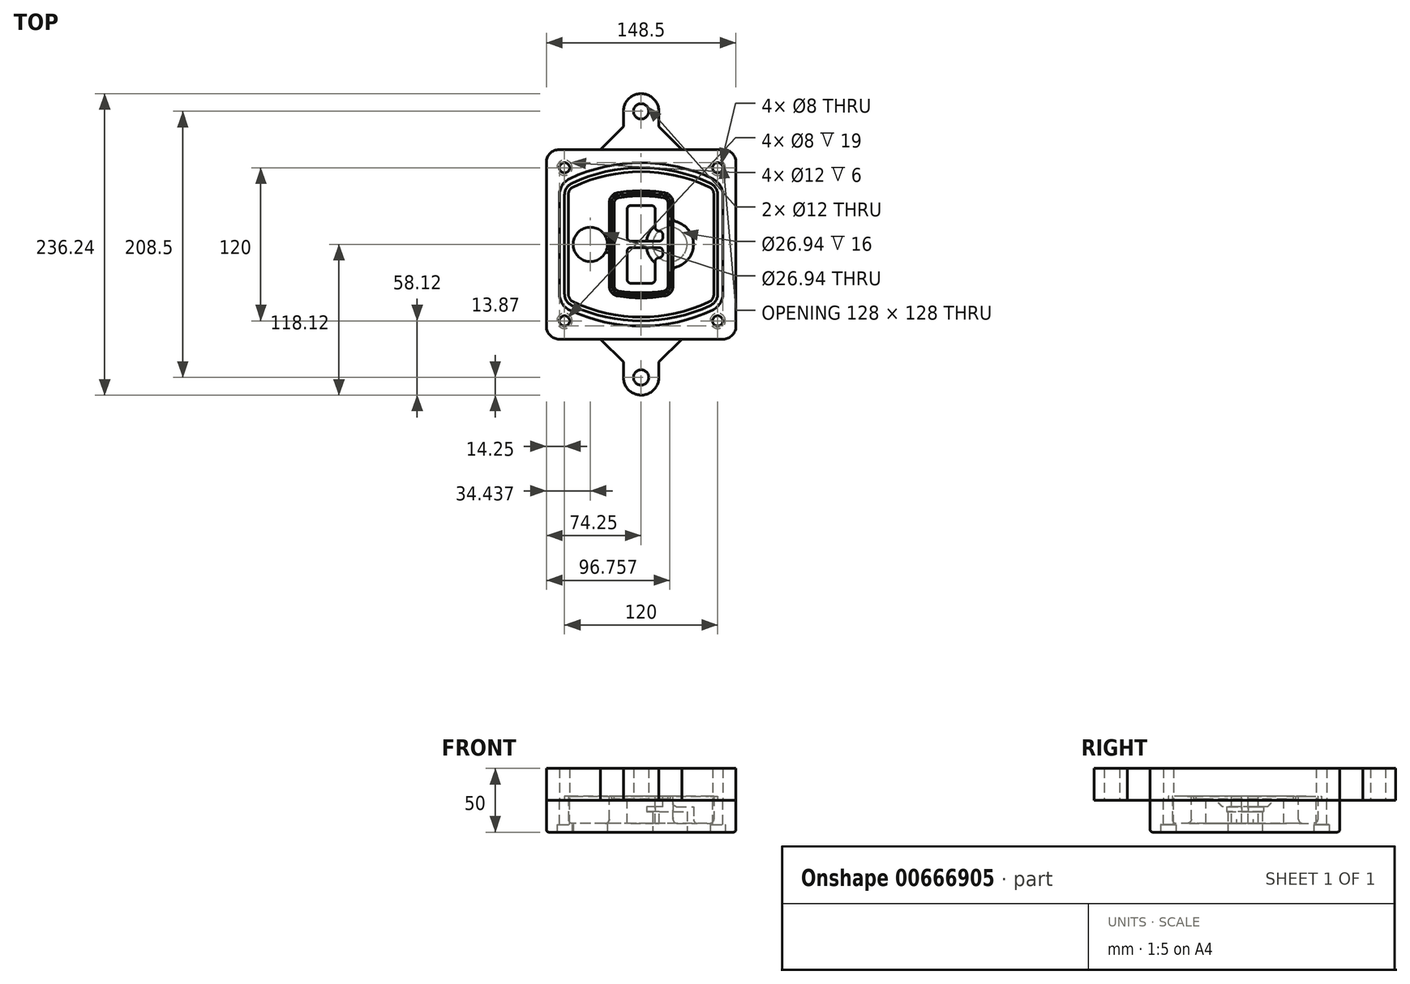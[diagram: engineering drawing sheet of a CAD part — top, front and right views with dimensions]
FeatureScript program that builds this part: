
annotation { "Feature Type Name" : "Feature", "Feature Type Description" : "" }
export const myFeature = defineFeature(function(context is Context, id is Id, definition is map)
    precondition{}
    {
        {
            var Q0;
            Q0=qCreatedBy(makeId("Top.planeOp"),FACE);
            var sketch = newSketch(context, id + "F0", { "sketchPlane" : qUnion([Q0])});
            skPoint(sketch, "E0.rect.middle", {"position": v(0, 0) * mm});
            skLineSegment(sketch, "E1.bottom", {"start": v(-64.25, -74.25) * mm, "end": v(64.25, -74.25) * mm});
            skLineSegment(sketch, "E1.top", {"start": v(-64.25, 74.25) * mm, "end": v(64.25, 74.25) * mm});
            skLineSegment(sketch, "E1.left", {"start": v(-74.25, -64.25) * mm, "end": v(-74.25, 64.25) * mm});
            skLineSegment(sketch, "E1.right", {"start": v(74.25, -64.25) * mm, "end": v(74.25, 64.25) * mm});
            skLineSegment(sketch, "E2", {"start": v(-74.25, 74.25) * mm, "end": v(74.25, -74.25) * mm, "construction": true});
            skLineSegment(sketch, "E3", {"start": v(74.25, 74.25) * mm, "end": v(-74.25, -74.25) * mm, "construction": true});
            skCircle(sketch, "E4", {"center": v(-60, 60) * mm, "radius": 4 * mm});
            skCircle(sketch, "E5", {"center": v(60, 60) * mm, "radius": 4 * mm});
            skCircle(sketch, "E6", {"center": v(60, -60) * mm, "radius": 4 * mm});
            skCircle(sketch, "E7", {"center": v(-60, -60) * mm, "radius": 4 * mm});
            skLineSegment(sketch, "E8", {"start": v(-60, 60) * mm, "end": v(60, 60) * mm, "construction": true});
            skLineSegment(sketch, "E9", {"start": v(60, 60) * mm, "end": v(60, -60) * mm, "construction": true});
            skLineSegment(sketch, "E10", {"start": v(60, -60) * mm, "end": v(-60, -60) * mm, "construction": true});
            skLineSegment(sketch, "E11", {"start": v(-60, -60) * mm, "end": v(-60, 60) * mm, "construction": true});
            skLineSegment(sketch, "E12", {"start": v(-60, 38.83) * mm, "end": v(-60, -38.83) * mm});
            skLineSegment(sketch, "E13", {"start": v(60, 38.83) * mm, "end": v(60, -38.83) * mm});
            skArc(sketch, "E14", {"start": v(54.26, 47.88) * mm, "mid": v(0, 60) * mm, "end": v(-54.26, 47.88) * mm});
            skArc(sketch, "E15", {"start": v(-54.26, -47.88) * mm, "mid": v(0, -60) * mm, "end": v(54.26, -47.88) * mm});
            skLineSegment(sketch, "E16", {"start": v(-60, 0) * mm, "end": v(60, 0) * mm, "construction": true});
            skPoint(sketch, "E17.visualSharp", {"position": v(-60, -45) * mm});
            skArc(sketch, "E17.filletArc", {"start": v(-60, -38.83) * mm, "mid": v(-58.44, -44.2) * mm, "end": v(-54.26, -47.88) * mm});
            skPoint(sketch, "E18.visualSharp", {"position": v(-60, 45) * mm});
            skArc(sketch, "E18.filletArc", {"start": v(-54.26, 47.88) * mm, "mid": v(-58.44, 44.2) * mm, "end": v(-60, 38.83) * mm});
            skPoint(sketch, "E19.visualSharp", {"position": v(60, 45) * mm});
            skArc(sketch, "E19.filletArc", {"start": v(60, 38.83) * mm, "mid": v(58.44, 44.2) * mm, "end": v(54.26, 47.88) * mm});
            skPoint(sketch, "E20.visualSharp", {"position": v(60, -45) * mm});
            skArc(sketch, "E20.filletArc", {"start": v(54.26, -47.88) * mm, "mid": v(58.44, -44.2) * mm, "end": v(60, -38.83) * mm});
            skPoint(sketch, "E21.visualSharp", {"position": v(-74.25, 74.25) * mm});
            skArc(sketch, "E21.filletArc", {"start": v(-64.25, 74.25) * mm, "mid": v(-71.32, 71.32) * mm, "end": v(-74.25, 64.25) * mm});
            skPoint(sketch, "E22.visualSharp", {"position": v(74.25, 74.25) * mm});
            skArc(sketch, "E22.filletArc", {"start": v(74.25, 64.25) * mm, "mid": v(71.32, 71.32) * mm, "end": v(64.25, 74.25) * mm});
            skPoint(sketch, "E23.visualSharp", {"position": v(74.25, -74.25) * mm});
            skArc(sketch, "E23.filletArc", {"start": v(64.25, -74.25) * mm, "mid": v(71.32, -71.32) * mm, "end": v(74.25, -64.25) * mm});
            skPoint(sketch, "E24.visualSharp", {"position": v(-74.25, -74.25) * mm});
            skArc(sketch, "E24.filletArc", {"start": v(-74.25, -64.25) * mm, "mid": v(-71.32, -71.32) * mm, "end": v(-64.25, -74.25) * mm});
            skArc(sketch, "E25.0", {"start": v(57, 38.83) * mm, "mid": v(55.9, 42.58) * mm, "end": v(52.98, 45.17) * mm});
            skLineSegment(sketch, "E25.1", {"start": v(57, 38.83) * mm, "end": v(57, -38.83) * mm});
            skArc(sketch, "E25.2", {"start": v(52.98, -45.17) * mm, "mid": v(55.9, -42.58) * mm, "end": v(57, -38.83) * mm});
            skArc(sketch, "E25.3", {"start": v(-52.98, -45.17) * mm, "mid": v(0, -57) * mm, "end": v(52.98, -45.17) * mm});
            skArc(sketch, "E25.4", {"start": v(-57, -38.83) * mm, "mid": v(-55.9, -42.58) * mm, "end": v(-52.98, -45.17) * mm});
            skArc(sketch, "E25.5", {"start": v(52.98, 45.17) * mm, "mid": v(0, 57) * mm, "end": v(-52.98, 45.17) * mm});
            skLineSegment(sketch, "E25.6", {"start": v(-57, 38.83) * mm, "end": v(-57, -38.83) * mm});
            skArc(sketch, "E25.7", {"start": v(-52.98, 45.17) * mm, "mid": v(-55.9, 42.58) * mm, "end": v(-57, 38.83) * mm});
            skArc(sketch, "E26.0", {"start": v(-55.96, 51.5) * mm, "mid": v(-61.82, 46.33) * mm, "end": v(-64, 38.83) * mm});
            skArc(sketch, "E26.1", {"start": v(55.96, 51.5) * mm, "mid": v(0, 64) * mm, "end": v(-55.96, 51.5) * mm});
            skArc(sketch, "E26.2", {"start": v(64, 38.83) * mm, "mid": v(61.82, 46.33) * mm, "end": v(55.96, 51.5) * mm});
            skLineSegment(sketch, "E26.3", {"start": v(64, 38.83) * mm, "end": v(64, -38.83) * mm});
            skArc(sketch, "E26.4", {"start": v(55.96, -51.5) * mm, "mid": v(61.82, -46.33) * mm, "end": v(64, -38.83) * mm});
            skLineSegment(sketch, "E26.5", {"start": v(-64, 38.83) * mm, "end": v(-64, -38.83) * mm});
            skArc(sketch, "E26.6", {"start": v(-55.96, -51.5) * mm, "mid": v(0, -64) * mm, "end": v(55.96, -51.5) * mm});
            skArc(sketch, "E26.7", {"start": v(-64, -38.83) * mm, "mid": v(-61.82, -46.33) * mm, "end": v(-55.96, -51.5) * mm});
            skSolve(sketch);
        }
        {
            var Q0;
            Q0=makeQuery(id+"F0.imprint","IMPRINT",FACE,{"disambiguationData":[TD([[makeQuery(id+"F0.imprint","IMPRINT",EDGE,{"derivedFrom":sQuery(id+"F0.wireOp",EDGE,"E1.bottom")}),1.0]])]});
            var Q1;
            Q1=makeQuery(id+"F0.imprint","IMPRINT",FACE,{"disambiguationData":[TD([[makeQuery(id+"F0.imprint","IMPRINT",EDGE,{"derivedFrom":sQuery(id+"F0.wireOp",EDGE,"E12")}),1.0]])]});
            var Q2;
            Q2=makeQuery(id+"F0.imprint","IMPRINT",FACE,{"disambiguationData":[TD([[makeQuery(id+"F0.imprint","IMPRINT",EDGE,{"derivedFrom":sQuery(id+"F0.wireOp",EDGE,"E25.0")}),1.0]])]});
            var Q3;
            Q3=makeQuery(id+"F0.imprint","IMPRINT",FACE,{"disambiguationData":[TD([[makeQuery(id+"F0.imprint","IMPRINT",EDGE,{"derivedFrom":sQuery(id+"F0.wireOp",EDGE,"E12")}),-1.0]])]});
            extrude(context, id + "F1", {"entities" : qUnion([Q0, Q1, Q2, Q3]), "oppositeDirection" : true, "depth" : 25 * mm});
        }
        {
            var Q0;
            Q0=makeQuery(id+"F0.imprint","IMPRINT",FACE,{"disambiguationData":[TD([[makeQuery(id+"F0.imprint","IMPRINT",EDGE,{"derivedFrom":sQuery(id+"F0.wireOp",EDGE,"E12")}),1.0]])]});
            extrude(context, id + "F2", {"entities" : qUnion([Q0]), "operationType" : NewBodyOperationType.ADD, "depth" : 3 * mm});
        }
        {
            var Q0;
            Q0=makeQuery(id+"F0.imprint","IMPRINT",FACE,{"disambiguationData":[TD([[makeQuery(id+"F0.imprint","IMPRINT",EDGE,{"derivedFrom":sQuery(id+"F0.wireOp",EDGE,"E25.0")}),1.0]])]});
            extrude(context, id + "F3", {"entities" : qUnion([Q0]), "operationType" : NewBodyOperationType.REMOVE, "oppositeDirection" : true, "depth" : 18 * mm});
        }
        {
            var Q0;
            Q0=makeQuery(id+"F2.opExtrude","CAP_FACE",FACE,{"disambiguationData":[OSD([sQuery(id+"F0.wireOp",EDGE,"E12"),sQuery(id+"F0.wireOp",EDGE,"E13"),sQuery(id+"F0.wireOp",EDGE,"E14"),sQuery(id+"F0.wireOp",EDGE,"E15"),sQuery(id+"F0.wireOp",EDGE,"E17.filletArc"),sQuery(id+"F0.wireOp",EDGE,"E18.filletArc"),sQuery(id+"F0.wireOp",EDGE,"E19.filletArc"),sQuery(id+"F0.wireOp",EDGE,"E20.filletArc"),sQuery(id+"F0.wireOp",EDGE,"E25.0"),sQuery(id+"F0.wireOp",EDGE,"E25.1"),sQuery(id+"F0.wireOp",EDGE,"E25.2"),sQuery(id+"F0.wireOp",EDGE,"E25.3"),sQuery(id+"F0.wireOp",EDGE,"E25.4"),sQuery(id+"F0.wireOp",EDGE,"E25.5"),sQuery(id+"F0.wireOp",EDGE,"E25.6"),sQuery(id+"F0.wireOp",EDGE,"E25.7")])],"isStart":false});
            var sketch = newSketch(context, id + "F4", { "sketchPlane" : qUnion([Q0])});
            skArc(sketch, "E27.0", {"start": v(-18.34, -40.45) * mm, "mid": v(0, -42) * mm, "end": v(18.34, -40.45) * mm});
            skArc(sketch, "E28.0", {"start": v(18.34, 40.45) * mm, "mid": v(0, 42) * mm, "end": v(-18.34, 40.45) * mm});
            skLineSegment(sketch, "E29", {"start": v(-25, 32.57) * mm, "end": v(-25, -32.57) * mm});
            skLineSegment(sketch, "E30", {"start": v(25, 32.57) * mm, "end": v(25, -32.57) * mm});
            skLineSegment(sketch, "E31", {"start": v(-25, 39.1) * mm, "end": v(25, 39.1) * mm, "construction": true});
            skLineSegment(sketch, "E32", {"start": v(-25, -39.1) * mm, "end": v(25, -39.1) * mm, "construction": true});
            skPoint(sketch, "E33.visualSharp", {"position": v(-25, 39.1) * mm});
            skArc(sketch, "E33.filletArc", {"start": v(-18.34, 40.45) * mm, "mid": v(-23.11, 37.73) * mm, "end": v(-25, 32.57) * mm});
            skPoint(sketch, "E34.visualSharp", {"position": v(25, 39.1) * mm});
            skArc(sketch, "E34.filletArc", {"start": v(25, 32.57) * mm, "mid": v(23.11, 37.73) * mm, "end": v(18.34, 40.45) * mm});
            skPoint(sketch, "E35.visualSharp", {"position": v(25, -39.1) * mm});
            skArc(sketch, "E35.filletArc", {"start": v(18.34, -40.45) * mm, "mid": v(23.11, -37.73) * mm, "end": v(25, -32.57) * mm});
            skPoint(sketch, "E36.visualSharp", {"position": v(-25, -39.1) * mm});
            skArc(sketch, "E36.filletArc", {"start": v(-25, -32.57) * mm, "mid": v(-23.11, -37.73) * mm, "end": v(-18.34, -40.45) * mm});
            skArc(sketch, "E37.0", {"start": v(52.98, 45.17) * mm, "mid": v(0, 57) * mm, "end": v(-52.98, 45.17) * mm});
            skArc(sketch, "E37.1", {"start": v(-52.98, 45.17) * mm, "mid": v(-55.9, 42.58) * mm, "end": v(-57, 38.83) * mm});
            skLineSegment(sketch, "E37.2", {"start": v(-57, 38.83) * mm, "end": v(-57, -38.83) * mm});
            skArc(sketch, "E37.3", {"start": v(-57, -38.83) * mm, "mid": v(-55.9, -42.58) * mm, "end": v(-52.98, -45.17) * mm});
            skArc(sketch, "E37.4", {"start": v(-52.98, -45.17) * mm, "mid": v(0, -57) * mm, "end": v(52.98, -45.17) * mm});
            skArc(sketch, "E37.5", {"start": v(52.98, -45.17) * mm, "mid": v(55.9, -42.58) * mm, "end": v(57, -38.83) * mm});
            skLineSegment(sketch, "E37.6", {"start": v(57, 38.83) * mm, "end": v(57, -38.83) * mm});
            skArc(sketch, "E37.7", {"start": v(57, 38.83) * mm, "mid": v(55.9, 42.58) * mm, "end": v(52.98, 45.17) * mm});
            skLineSegment(sketch, "E38.0", {"start": v(23, 32.57) * mm, "end": v(23, -32.57) * mm});
            skArc(sketch, "E38.1", {"start": v(18, -38.48) * mm, "mid": v(21.58, -36.44) * mm, "end": v(23, -32.57) * mm});
            skArc(sketch, "E38.2", {"start": v(-18, -38.48) * mm, "mid": v(0, -40) * mm, "end": v(18, -38.48) * mm});
            skArc(sketch, "E38.3", {"start": v(-23, -32.57) * mm, "mid": v(-21.58, -36.44) * mm, "end": v(-18, -38.48) * mm});
            skLineSegment(sketch, "E38.4", {"start": v(-23, 32.57) * mm, "end": v(-23, -32.57) * mm});
            skArc(sketch, "E38.5", {"start": v(23, 32.57) * mm, "mid": v(21.58, 36.44) * mm, "end": v(18, 38.48) * mm});
            skArc(sketch, "E38.6", {"start": v(-18, 38.48) * mm, "mid": v(-21.58, 36.44) * mm, "end": v(-23, 32.57) * mm});
            skArc(sketch, "E38.7", {"start": v(18, 38.48) * mm, "mid": v(0, 40) * mm, "end": v(-18, 38.48) * mm});
            skArc(sketch, "E39.0", {"start": v(21, 32.57) * mm, "mid": v(20.06, 35.15) * mm, "end": v(17.67, 36.5) * mm});
            skLineSegment(sketch, "E39.1", {"start": v(21, 32.57) * mm, "end": v(21, -32.57) * mm});
            skArc(sketch, "E39.2", {"start": v(17.67, -36.5) * mm, "mid": v(20.06, -35.15) * mm, "end": v(21, -32.57) * mm});
            skArc(sketch, "E39.3", {"start": v(-17.67, -36.5) * mm, "mid": v(0, -38) * mm, "end": v(17.67, -36.5) * mm});
            skArc(sketch, "E39.4", {"start": v(-21, -32.57) * mm, "mid": v(-20.06, -35.15) * mm, "end": v(-17.67, -36.5) * mm});
            skArc(sketch, "E39.5", {"start": v(17.67, 36.5) * mm, "mid": v(0, 38) * mm, "end": v(-17.67, 36.5) * mm});
            skLineSegment(sketch, "E39.6", {"start": v(-21, 32.57) * mm, "end": v(-21, -32.57) * mm});
            skArc(sketch, "E39.7", {"start": v(-17.67, 36.5) * mm, "mid": v(-20.06, 35.15) * mm, "end": v(-21, 32.57) * mm});
            skLineSegment(sketch, "E40", {"start": v(-25, 0) * mm, "end": v(25, 0) * mm, "construction": true});
            skLineSegment(sketch, "E41", {"start": v(-11, 5.5) * mm, "end": v(-11, 27.5) * mm});
            skLineSegment(sketch, "E42", {"start": v(-8, 30.5) * mm, "end": v(8, 30.5) * mm});
            skLineSegment(sketch, "E43", {"start": v(11, 27.5) * mm, "end": v(11, 13.5) * mm});
            skLineSegment(sketch, "E44", {"start": v(14, 10.5) * mm, "end": v(14, 10.5) * mm});
            skLineSegment(sketch, "E45", {"start": v(17, 7.5) * mm, "end": v(17, 5.5) * mm});
            skLineSegment(sketch, "E46", {"start": v(14, 2.5) * mm, "end": v(-8, 2.5) * mm});
            skPoint(sketch, "E47.visualSharp", {"position": v(-11, 30.5) * mm});
            skArc(sketch, "E47.filletArc", {"start": v(-8, 30.5) * mm, "mid": v(-10.12, 29.62) * mm, "end": v(-11, 27.5) * mm});
            skPoint(sketch, "E48.visualSharp", {"position": v(11, 30.5) * mm});
            skArc(sketch, "E48.filletArc", {"start": v(11, 27.5) * mm, "mid": v(10.12, 29.62) * mm, "end": v(8, 30.5) * mm});
            skPoint(sketch, "E49.visualSharp", {"position": v(11, 10.5) * mm});
            skArc(sketch, "E49.filletArc", {"start": v(11, 13.5) * mm, "mid": v(11.88, 11.38) * mm, "end": v(14, 10.5) * mm});
            skPoint(sketch, "E50.visualSharp", {"position": v(17, 10.5) * mm});
            skArc(sketch, "E50.filletArc", {"start": v(17, 7.5) * mm, "mid": v(16.12, 9.62) * mm, "end": v(14, 10.5) * mm});
            skPoint(sketch, "E51.visualSharp", {"position": v(17, 2.5) * mm});
            skArc(sketch, "E51.filletArc", {"start": v(14, 2.5) * mm, "mid": v(16.12, 3.38) * mm, "end": v(17, 5.5) * mm});
            skPoint(sketch, "E52.visualSharp", {"position": v(-11, 2.5) * mm});
            skArc(sketch, "E52.filletArc", {"start": v(-11, 5.5) * mm, "mid": v(-10.12, 3.38) * mm, "end": v(-8, 2.5) * mm});
            skLineSegment(sketch, "E53.0.MirrorCS", {"start": v(14, -2.5) * mm, "end": v(-8, -2.5) * mm});
            skArc(sketch, "E54.0.MirrorCS", {"start": v(-11, -5.5) * mm, "mid": v(-10.12, -3.38) * mm, "end": v(-8, -2.5) * mm});
            skLineSegment(sketch, "E55.0.MirrorCS", {"start": v(-11, -5.5) * mm, "end": v(-11, -27.5) * mm});
            skArc(sketch, "E56.0.MirrorCS", {"start": v(-8, -30.5) * mm, "mid": v(-10.12, -29.62) * mm, "end": v(-11, -27.5) * mm});
            skLineSegment(sketch, "E57.0.MirrorCS", {"start": v(-8, -30.5) * mm, "end": v(8, -30.5) * mm});
            skArc(sketch, "E58.0.MirrorCS", {"start": v(11, -27.5) * mm, "mid": v(10.12, -29.62) * mm, "end": v(8, -30.5) * mm});
            skLineSegment(sketch, "E59.0.MirrorCS", {"start": v(11, -27.5) * mm, "end": v(11, -13.5) * mm});
            skArc(sketch, "E60.0.MirrorCS", {"start": v(11, -13.5) * mm, "mid": v(11.88, -11.38) * mm, "end": v(14, -10.5) * mm});
            skArc(sketch, "E61.0.MirrorCS", {"start": v(17, -7.5) * mm, "mid": v(16.12, -9.62) * mm, "end": v(14, -10.5) * mm});
            skLineSegment(sketch, "E62.0.MirrorCS", {"start": v(17, -7.5) * mm, "end": v(17, -5.5) * mm});
            skArc(sketch, "E63.0.MirrorCS", {"start": v(14, -2.5) * mm, "mid": v(16.12, -3.38) * mm, "end": v(17, -5.5) * mm});
            skSolve(sketch);
        }
        {
            var Q0;
            Q0=makeQuery(id+"F4.imprint","IMPRINT",FACE,{"disambiguationData":[TD([[makeQuery(id+"F4.imprint","IMPRINT",EDGE,{"derivedFrom":sQuery(id+"F4.wireOp",EDGE,"E27.0")}),1.0]])]});
            var Q1;
            Q1=makeQuery(id+"F4.imprint","IMPRINT",FACE,{"disambiguationData":[TD([[makeQuery(id+"F4.imprint","IMPRINT",EDGE,{"derivedFrom":sQuery(id+"F4.wireOp",EDGE,"E38.0")}),-1.0]])]});
            var Q2;
            Q2=makeQuery(id+"F4.imprint","IMPRINT",FACE,{"disambiguationData":[TD([[makeQuery(id+"F4.imprint","IMPRINT",EDGE,{"derivedFrom":sQuery(id+"F4.wireOp",EDGE,"E39.0")}),1.0]])]});
            extrude(context, id + "F5", {"entities" : qUnion([Q0, Q1, Q2]), "operationType" : NewBodyOperationType.ADD, "endBound" : BoundingType.UP_TO_NEXT, "oppositeDirection" : true, "depth" : 25 * mm});
        }
        {
            var Q0;
            Q0=makeQuery(id+"F4.imprint","IMPRINT",FACE,{"disambiguationData":[TD([[makeQuery(id+"F4.imprint","IMPRINT",EDGE,{"derivedFrom":sQuery(id+"F4.wireOp",EDGE,"E38.0")}),-1.0]])]});
            extrude(context, id + "F6", {"entities" : qUnion([Q0]), "operationType" : NewBodyOperationType.REMOVE, "oppositeDirection" : true, "depth" : 2 * mm});
        }
        {
            var Q0;
            Q0=makeQuery(id+"F1.opExtrude","CAP_FACE",FACE,{"disambiguationData":[OSD([sQuery(id+"F0.wireOp",EDGE,"E1.bottom"),sQuery(id+"F0.wireOp",EDGE,"E1.top"),sQuery(id+"F0.wireOp",EDGE,"E1.left"),sQuery(id+"F0.wireOp",EDGE,"E1.right"),sQuery(id+"F0.wireOp",EDGE,"E4"),sQuery(id+"F0.wireOp",EDGE,"E5"),sQuery(id+"F0.wireOp",EDGE,"E6"),sQuery(id+"F0.wireOp",EDGE,"E7"),sQuery(id+"F0.wireOp",EDGE,"E21.filletArc"),sQuery(id+"F0.wireOp",EDGE,"E22.filletArc"),sQuery(id+"F0.wireOp",EDGE,"E23.filletArc"),sQuery(id+"F0.wireOp",EDGE,"E24.filletArc")])],"isStart":false});
            var sketch = newSketch(context, id + "F7", { "sketchPlane" : qUnion([Q0])});
            skCircle(sketch, "E64", {"center": v(22.5, 0) * mm, "radius": 13.47 * mm});
            skCircle(sketch, "E65", {"center": v(-39.81, 0) * mm, "radius": 13.47 * mm});
            skLineSegment(sketch, "E66", {"start": v(74.25, 0) * mm, "end": v(-74.25, 0) * mm});
            skCircle(sketch, "E67", {"center": v(22.5, 0) * mm, "radius": 18.47 * mm});
            skCircle(sketch, "E68", {"center": v(60, -60) * mm, "radius": 6 * mm});
            skCircle(sketch, "E69", {"center": v(-60, -60) * mm, "radius": 6 * mm});
            skCircle(sketch, "E70", {"center": v(-60, 60) * mm, "radius": 6 * mm});
            skCircle(sketch, "E71", {"center": v(60, 60) * mm, "radius": 6 * mm});
            skSolve(sketch);
        }
        {
            var Q0;
            {var subQ1=sQuery(id+"F7.wireOp",EDGE,"E66");var subQ4=sQuery(id+"F7.wireOp",EDGE,"E64");var subQ6=makeQuery(id+"F7.imprint","INTERSECT",VERTEX,{"disambiguationData":[OD(0.0)],"derivedFrom":[subQ4,subQ1]});Q0=makeQuery(id+"F7.imprint","IMPRINT",FACE,{"disambiguationData":[TD([[makeQuery(id+"F7.imprint","IMPRINT",EDGE,{"disambiguationData":[TD([[subQ6,-1.0]])],"derivedFrom":subQ4}),-1.0]])]});}
            var Q1;
            {var subQ0=sQuery(id+"F7.wireOp",EDGE,"E66");var subQ1=sQuery(id+"F7.wireOp",EDGE,"E64");var subQ3=makeQuery(id+"F7.imprint","INTERSECT",VERTEX,{"disambiguationData":[OD(0.0)],"derivedFrom":[subQ1,subQ0]});Q1=makeQuery(id+"F7.imprint","IMPRINT",FACE,{"disambiguationData":[TD([[makeQuery(id+"F7.imprint","IMPRINT",EDGE,{"disambiguationData":[TD([[subQ3,-1.0]])],"derivedFrom":subQ1}),1.0]])]});}
            var Q2;
            {var subQ0=sQuery(id+"F7.wireOp",EDGE,"E66");var subQ1=sQuery(id+"F7.wireOp",EDGE,"E64");var subQ3=makeQuery(id+"F7.imprint","INTERSECT",VERTEX,{"disambiguationData":[OD(0.0)],"derivedFrom":[subQ1,subQ0]});Q2=makeQuery(id+"F7.imprint","IMPRINT",FACE,{"disambiguationData":[TD([[makeQuery(id+"F7.imprint","IMPRINT",EDGE,{"disambiguationData":[TD([[subQ3,1.0]])],"derivedFrom":subQ1}),1.0]])]});}
            var Q3;
            {var subQ1=sQuery(id+"F7.wireOp",EDGE,"E66");var subQ4=sQuery(id+"F7.wireOp",EDGE,"E64");var subQ6=makeQuery(id+"F7.imprint","INTERSECT",VERTEX,{"disambiguationData":[OD(0.0)],"derivedFrom":[subQ4,subQ1]});Q3=makeQuery(id+"F7.imprint","IMPRINT",FACE,{"disambiguationData":[TD([[makeQuery(id+"F7.imprint","IMPRINT",EDGE,{"disambiguationData":[TD([[subQ6,1.0]])],"derivedFrom":subQ4}),-1.0]])]});}
            extrude(context, id + "F8", {"entities" : qUnion([Q0, Q1, Q2, Q3]), "operationType" : NewBodyOperationType.ADD, "oppositeDirection" : true, "depth" : 20 * mm});
        }
        {
            var Q0;
            {var subQ0=sQuery(id+"F7.wireOp",EDGE,"E66");var subQ1=sQuery(id+"F7.wireOp",EDGE,"E64");var subQ3=makeQuery(id+"F7.imprint","INTERSECT",VERTEX,{"disambiguationData":[OD(0.0)],"derivedFrom":[subQ1,subQ0]});Q0=makeQuery(id+"F7.imprint","IMPRINT",FACE,{"disambiguationData":[TD([[makeQuery(id+"F7.imprint","IMPRINT",EDGE,{"disambiguationData":[TD([[subQ3,-1.0]])],"derivedFrom":subQ1}),1.0]])]});}
            var Q1;
            {var subQ0=sQuery(id+"F7.wireOp",EDGE,"E66");var subQ1=sQuery(id+"F7.wireOp",EDGE,"E64");var subQ3=makeQuery(id+"F7.imprint","INTERSECT",VERTEX,{"disambiguationData":[OD(0.0)],"derivedFrom":[subQ1,subQ0]});Q1=makeQuery(id+"F7.imprint","IMPRINT",FACE,{"disambiguationData":[TD([[makeQuery(id+"F7.imprint","IMPRINT",EDGE,{"disambiguationData":[TD([[subQ3,1.0]])],"derivedFrom":subQ1}),1.0]])]});}
            extrude(context, id + "F9", {"entities" : qUnion([Q0, Q1]), "operationType" : NewBodyOperationType.REMOVE, "oppositeDirection" : true, "depth" : 16 * mm});
        }
        {
            var Q0;
            {var subQ0=sQuery(id+"F7.wireOp",EDGE,"E66");var subQ1=sQuery(id+"F7.wireOp",EDGE,"E65");var subQ3=makeQuery(id+"F7.imprint","INTERSECT",VERTEX,{"disambiguationData":[OD(0.0)],"derivedFrom":[subQ1,subQ0]});Q0=makeQuery(id+"F7.imprint","IMPRINT",FACE,{"disambiguationData":[TD([[makeQuery(id+"F7.imprint","IMPRINT",EDGE,{"disambiguationData":[TD([[subQ3,-1.0]])],"derivedFrom":subQ1}),1.0]])]});}
            var Q1;
            {var subQ0=sQuery(id+"F7.wireOp",EDGE,"E66");var subQ1=sQuery(id+"F7.wireOp",EDGE,"E65");var subQ3=makeQuery(id+"F7.imprint","INTERSECT",VERTEX,{"disambiguationData":[OD(0.0)],"derivedFrom":[subQ1,subQ0]});Q1=makeQuery(id+"F7.imprint","IMPRINT",FACE,{"disambiguationData":[TD([[makeQuery(id+"F7.imprint","IMPRINT",EDGE,{"disambiguationData":[TD([[subQ3,1.0]])],"derivedFrom":subQ1}),1.0]])]});}
            extrude(context, id + "F10", {"entities" : qUnion([Q0, Q1]), "operationType" : NewBodyOperationType.REMOVE, "oppositeDirection" : true, "depth" : 25 * mm});
        }
        {
            var Q0;
            Q0=makeQuery(id+"F7.imprint","IMPRINT",FACE,{"disambiguationData":[TD([[makeQuery(id+"F7.imprint","IMPRINT",EDGE,{"derivedFrom":sQuery(id+"F7.wireOp",EDGE,"E68")}),1.0]])]});
            var Q1;
            Q1=makeQuery(id+"F7.imprint","IMPRINT",FACE,{"disambiguationData":[TD([[makeQuery(id+"F7.imprint","IMPRINT",EDGE,{"derivedFrom":makeQuery(id+"F1.opExtrude","CAP_EDGE",EDGE,{"disambiguationData":[OSD([sQuery(id+"F0.wireOp",EDGE,"E5")])],"isStart":false})}),-1.0]])]});
            var Q2;
            Q2=makeQuery(id+"F7.imprint","IMPRINT",FACE,{"disambiguationData":[TD([[makeQuery(id+"F7.imprint","IMPRINT",EDGE,{"derivedFrom":sQuery(id+"F7.wireOp",EDGE,"E69")}),1.0]])]});
            var Q3;
            Q3=makeQuery(id+"F7.imprint","IMPRINT",FACE,{"disambiguationData":[TD([[makeQuery(id+"F7.imprint","IMPRINT",EDGE,{"derivedFrom":makeQuery(id+"F1.opExtrude","CAP_EDGE",EDGE,{"disambiguationData":[OSD([sQuery(id+"F0.wireOp",EDGE,"E4")])],"isStart":false})}),-1.0]])]});
            var Q4;
            Q4=makeQuery(id+"F7.imprint","IMPRINT",FACE,{"disambiguationData":[TD([[makeQuery(id+"F7.imprint","IMPRINT",EDGE,{"derivedFrom":sQuery(id+"F7.wireOp",EDGE,"E70")}),1.0]])]});
            var Q5;
            Q5=makeQuery(id+"F7.imprint","IMPRINT",FACE,{"disambiguationData":[TD([[makeQuery(id+"F7.imprint","IMPRINT",EDGE,{"derivedFrom":makeQuery(id+"F1.opExtrude","CAP_EDGE",EDGE,{"disambiguationData":[OSD([sQuery(id+"F0.wireOp",EDGE,"E7")])],"isStart":false})}),-1.0]])]});
            var Q6;
            Q6=makeQuery(id+"F7.imprint","IMPRINT",FACE,{"disambiguationData":[TD([[makeQuery(id+"F7.imprint","IMPRINT",EDGE,{"derivedFrom":sQuery(id+"F7.wireOp",EDGE,"E71")}),1.0]])]});
            var Q7;
            Q7=makeQuery(id+"F7.imprint","IMPRINT",FACE,{"disambiguationData":[TD([[makeQuery(id+"F7.imprint","IMPRINT",EDGE,{"derivedFrom":makeQuery(id+"F1.opExtrude","CAP_EDGE",EDGE,{"disambiguationData":[OSD([sQuery(id+"F0.wireOp",EDGE,"E6")])],"isStart":false})}),-1.0]])]});
            extrude(context, id + "F11", {"entities" : qUnion([Q0, Q1, Q2, Q3, Q4, Q5, Q6, Q7]), "operationType" : NewBodyOperationType.REMOVE, "oppositeDirection" : true, "depth" : 6 * mm});
        }
        {
            var Q0;
            Q0=makeQuery(id+"F9.boolean.opBoolean","COPY",FACE,{"derivedFrom":makeQuery(id+"F9.opExtrude","CAP_FACE",FACE,{"disambiguationData":[OSD([sQuery(id+"F7.wireOp",EDGE,"E64")])],"isStart":false})});
            var sketch = newSketch(context, id + "F12", { "sketchPlane" : qUnion([Q0])});
            skArc(sketch, "E72.0", {"start": v(11, 14.45) * mm, "mid": v(6.45, 9.13) * mm, "end": v(4.2, 2.5) * mm});
            skArc(sketch, "E72.1", {"start": v(4.2, -2.5) * mm, "mid": v(6.45, -9.13) * mm, "end": v(11, -14.45) * mm});
            skLineSegment(sketch, "E73", {"start": v(4.2, -2.5) * mm, "end": v(14, -2.5) * mm});
            skLineSegment(sketch, "E74.0", {"start": v(14, 2.5) * mm, "end": v(4.2, 2.5) * mm});
            skArc(sketch, "E74.1", {"start": v(14, 2.5) * mm, "mid": v(16.12, 3.38) * mm, "end": v(17, 5.5) * mm});
            skLineSegment(sketch, "E74.2", {"start": v(17, 7.5) * mm, "end": v(17, 5.5) * mm});
            skArc(sketch, "E74.3", {"start": v(17, 7.5) * mm, "mid": v(16.12, 9.62) * mm, "end": v(14, 10.5) * mm});
            skArc(sketch, "E74.4", {"start": v(11, 13.5) * mm, "mid": v(11.88, 11.38) * mm, "end": v(14, 10.5) * mm});
            skLineSegment(sketch, "E74.5", {"start": v(11, 14.45) * mm, "end": v(11, 13.5) * mm});
            skLineSegment(sketch, "E74.7", {"start": v(14, -2.5) * mm, "end": v(4.2, -2.5) * mm});
            skArc(sketch, "E74.8", {"start": v(14, -2.5) * mm, "mid": v(16.12, -3.38) * mm, "end": v(17, -5.5) * mm});
            skLineSegment(sketch, "E74.9", {"start": v(17, -7.5) * mm, "end": v(17, -5.5) * mm});
            skArc(sketch, "E74.10", {"start": v(17, -7.5) * mm, "mid": v(16.12, -9.62) * mm, "end": v(14, -10.5) * mm});
            skArc(sketch, "E74.11", {"start": v(11, -13.5) * mm, "mid": v(11.88, -11.38) * mm, "end": v(14, -10.5) * mm});
            skLineSegment(sketch, "E74.12", {"start": v(11, -14.45) * mm, "end": v(11, -13.5) * mm});
            skPoint(sketch, "E75.orphan", {"position": v(11, -27.5) * mm});
            skPoint(sketch, "E76.orphan", {"position": v(-8, -2.5) * mm});
            skPoint(sketch, "E77.orphan", {"position": v(-8, 2.5) * mm});
            skPoint(sketch, "E78.orphan", {"position": v(11, 27.5) * mm});
            skSolve(sketch);
        }
        {
            var Q0;
            {var subQ7=sQuery(id+"F12.wireOp",EDGE,"E72.0");var subQ14=sQuery(id+"F12.wireOp",EDGE,"E72.1");var subQ16=sQuery(id+"F12.wireOp",EDGE,"E74.1");var subQ18=sQuery(id+"F12.wireOp",EDGE,"E74.8");Q0=qUnion([makeQuery(id+"F12.imprint","IMPRINT",FACE,{"disambiguationData":[TD([[makeQuery(id+"F12.imprint","IMPRINT",EDGE,{"derivedFrom":subQ7}),1.0]])]}),makeQuery(id+"F12.imprint","IMPRINT",FACE,{"disambiguationData":[TD([[makeQuery(id+"F12.imprint","IMPRINT",EDGE,{"derivedFrom":subQ14}),1.0]])]}),makeQuery(id+"F12.imprint","IMPRINT",FACE,{"disambiguationData":[TD([[makeQuery(id+"F12.imprint","IMPRINT",EDGE,{"derivedFrom":subQ16}),1.0]])]}),makeQuery(id+"F12.imprint","IMPRINT",FACE,{"disambiguationData":[TD([[makeQuery(id+"F12.imprint","IMPRINT",EDGE,{"derivedFrom":subQ18}),-1.0]])]})]);}
            var Q1;
            Q1=makeQuery(id+"F5.boolean.opBoolean","SPLIT",FACE,{"disambiguationData":[TD([makeQuery(id+"F5.opExtrude","SWEPT_FACE",FACE,{"disambiguationData":[OSD([sQuery(id+"F4.wireOp",EDGE,"E41")])]})])],"derivedFrom":makeQuery(id+"F3.boolean.opBoolean","COPY",FACE,{"derivedFrom":makeQuery(id+"F3.opExtrude","CAP_FACE",FACE,{"disambiguationData":[OSD([sQuery(id+"F0.wireOp",EDGE,"E25.0"),sQuery(id+"F0.wireOp",EDGE,"E25.1"),sQuery(id+"F0.wireOp",EDGE,"E25.2"),sQuery(id+"F0.wireOp",EDGE,"E25.3"),sQuery(id+"F0.wireOp",EDGE,"E25.4"),sQuery(id+"F0.wireOp",EDGE,"E25.5"),sQuery(id+"F0.wireOp",EDGE,"E25.6"),sQuery(id+"F0.wireOp",EDGE,"E25.7")])],"isStart":false})})});
            extrude(context, id + "F13", {"entities" : qUnion([Q0]), "operationType" : NewBodyOperationType.REMOVE, "endBound" : BoundingType.UP_TO_SURFACE, "endBoundEntityFace" : qUnion([Q1]), "depth" : 25 * mm});
        }
        {
            var Q0;
            Q0=makeQuery(id+"F3.boolean.opBoolean","COPY",EDGE,{"derivedFrom":makeQuery(id+"F3.opExtrude","CAP_EDGE",EDGE,{"disambiguationData":[OSD([sQuery(id+"F0.wireOp",EDGE,"E25.6")])],"isStart":false})});
            var Q1;
            Q1=makeQuery(id+"F8.boolean.opBoolean","INTERSECT",EDGE,{"derivedFrom":[makeQuery(id+"F5.opExtrude","SWEPT_FACE",FACE,{"disambiguationData":[OSD([sQuery(id+"F4.wireOp",EDGE,"E30")])]}),makeQuery(id+"F8.opExtrude","CAP_FACE",FACE,{"disambiguationData":[OSD([sQuery(id+"F7.wireOp",EDGE,"E67")])],"isStart":false})]});
            var Q2;
            Q2=makeQuery(id+"F8.boolean.opBoolean","INTERSECT",EDGE,{"disambiguationData":[OD(1.0)],"derivedFrom":[makeQuery(id+"F5.opExtrude","SWEPT_FACE",FACE,{"disambiguationData":[OSD([sQuery(id+"F4.wireOp",EDGE,"E30")])]}),makeQuery(id+"F8.opExtrude","SWEPT_FACE",FACE,{"disambiguationData":[OSD([sQuery(id+"F7.wireOp",EDGE,"E67")])]})]});
            var Q3;
            {var subQ0=sQuery(id+"F4.wireOp",EDGE,"E30");Q3=makeQuery(id+"F8.boolean.opBoolean","SPLIT",EDGE,{"disambiguationData":[TD([makeQuery(id+"F5.opExtrude","SWEPT_FACE",FACE,{"disambiguationData":[OSD([sQuery(id+"F4.wireOp",EDGE,"E35.filletArc")])]})])],"derivedFrom":makeQuery(id+"F5.opExtrude","CAP_EDGE",EDGE,{"disambiguationData":[OSD([subQ0])],"isStart":false})});}
            var Q4;
            {var subQ0=sQuery(id+"F0.wireOp",EDGE,"E25.7");var subQ1=sQuery(id+"F0.wireOp",EDGE,"E25.1");var subQ2=sQuery(id+"F0.wireOp",EDGE,"E25.6");var subQ3=sQuery(id+"F0.wireOp",EDGE,"E25.5");var subQ4=sQuery(id+"F0.wireOp",EDGE,"E25.4");var subQ5=sQuery(id+"F0.wireOp",EDGE,"E25.0");var subQ6=sQuery(id+"F0.wireOp",EDGE,"E25.2");var subQ7=sQuery(id+"F0.wireOp",EDGE,"E25.3");Q4=makeQuery(id+"F8.boolean.opBoolean","INTERSECT",EDGE,{"derivedFrom":[makeQuery(id+"F5.boolean.opBoolean","SPLIT",FACE,{"disambiguationData":[TD([makeQuery(id+"F2.opExtrude","SWEPT_FACE",FACE,{"disambiguationData":[OSD([subQ5])]})])],"derivedFrom":makeQuery(id+"F3.boolean.opBoolean","COPY",FACE,{"derivedFrom":makeQuery(id+"F3.opExtrude","CAP_FACE",FACE,{"disambiguationData":[OSD([subQ5,subQ1,subQ6,subQ7,subQ4,subQ3,subQ2,subQ0])],"isStart":false})})}),makeQuery(id+"F8.opExtrude","SWEPT_FACE",FACE,{"disambiguationData":[OSD([sQuery(id+"F7.wireOp",EDGE,"E67")])]})]});}
            var Q5;
            Q5=makeQuery(id+"F8.boolean.opBoolean","INTERSECT",EDGE,{"disambiguationData":[OD(0.0)],"derivedFrom":[makeQuery(id+"F5.opExtrude","SWEPT_FACE",FACE,{"disambiguationData":[OSD([sQuery(id+"F4.wireOp",EDGE,"E30")])]}),makeQuery(id+"F8.opExtrude","SWEPT_FACE",FACE,{"disambiguationData":[OSD([sQuery(id+"F7.wireOp",EDGE,"E67")])]})]});
            fillet(context, id + "F14", {"entities" : qUnion([Q0, Q1, Q2, Q3, Q4, Q5]), "radius" : 3 * mm, "tangentPropagation" : true, "allowEdgeOverflow" : false});
        }
        {
            var Q0;
            Q0=makeQuery(id+"F1.opExtrude","CAP_EDGE",EDGE,{"disambiguationData":[OSD([sQuery(id+"F0.wireOp",EDGE,"E1.bottom")])],"isStart":false});
            fillet(context, id + "F15", {"entities" : qUnion([Q0]), "radius" : 2 * mm, "tangentPropagation" : true, "allowEdgeOverflow" : false});
        }
        {
            var Q0;
            {var subQ0=sQuery(id+"F0.wireOp",EDGE,"E21.filletArc");var subQ1=sQuery(id+"F0.wireOp",EDGE,"E7");var subQ2=sQuery(id+"F0.wireOp",EDGE,"E6");var subQ3=sQuery(id+"F0.wireOp",EDGE,"E5");var subQ4=sQuery(id+"F0.wireOp",EDGE,"E4");var subQ5=sQuery(id+"F0.wireOp",EDGE,"E22.filletArc");var subQ6=sQuery(id+"F0.wireOp",EDGE,"E1.bottom");var subQ7=sQuery(id+"F0.wireOp",EDGE,"E1.right");var subQ8=sQuery(id+"F0.wireOp",EDGE,"E1.top");var subQ9=sQuery(id+"F0.wireOp",EDGE,"E1.left");var subQ10=sQuery(id+"F0.wireOp",EDGE,"E23.filletArc");var subQ11=sQuery(id+"F0.wireOp",EDGE,"E24.filletArc");Q0=makeQuery(id+"F2.boolean.opBoolean","SPLIT",FACE,{"disambiguationData":[TD([makeQuery(id+"F1.opExtrude","SWEPT_FACE",FACE,{"disambiguationData":[OSD([subQ6])]})])],"derivedFrom":makeQuery(id+"F1.opExtrude","CAP_FACE",FACE,{"disambiguationData":[OSD([subQ6,subQ8,subQ9,subQ7,subQ4,subQ3,subQ2,subQ1,subQ0,subQ5,subQ10,subQ11])],"isStart":true})});}
            var sketch = newSketch(context, id + "F16", { "sketchPlane" : qUnion([Q0])});
            skCircle(sketch, "E79", {"center": v(0, 104.25) * mm, "radius": 6 * mm});
            skLineSegment(sketch, "E80", {"start": v(-31.87, 74.25) * mm, "end": v(-13.87, 92.25) * mm});
            skPoint(sketch, "E81", {"position": v(0, 74.25) * mm});
            skPoint(sketch, "E82", {"position": v(0, 92.25) * mm});
            skLineSegment(sketch, "E83", {"start": v(31.87, 74.25) * mm, "end": v(13.87, 92.25) * mm});
            skLineSegment(sketch, "E84", {"start": v(-13.87, 92.25) * mm, "end": v(-13.87, 104.23) * mm});
            skLineSegment(sketch, "E85", {"start": v(13.87, 92.25) * mm, "end": v(13.87, 104.23) * mm});
            skArc(sketch, "E86", {"start": v(13.87, 104.23) * mm, "mid": v(-0.04, 118.12) * mm, "end": v(-13.87, 104.14) * mm});
            skPoint(sketch, "E87", {"position": v(-97.77, 0) * mm});
            skPoint(sketch, "E88", {"position": v(97.95, 0) * mm});
            skLineSegment(sketch, "E89.MirrorCS", {"start": v(-31.87, -74.25) * mm, "end": v(-13.87, -92.25) * mm});
            skLineSegment(sketch, "E90.MirrorCS", {"start": v(-13.87, -92.25) * mm, "end": v(-13.87, -104.23) * mm});
            skArc(sketch, "E91.MirrorCS", {"start": v(13.87, -104.23) * mm, "mid": v(-0.04, -118.12) * mm, "end": v(-13.87, -104.14) * mm});
            skLineSegment(sketch, "E92.MirrorCS", {"start": v(31.87, -74.25) * mm, "end": v(13.87, -92.25) * mm});
            skLineSegment(sketch, "E93.MirrorCS", {"start": v(13.87, -92.25) * mm, "end": v(13.87, -104.23) * mm});
            skCircle(sketch, "E94.MirrorC", {"center": v(0, -104.25) * mm, "radius": 6 * mm});
            skSolve(sketch);
        }
        {
            var Q0;
            Q0=makeQuery(id+"F0.imprint","IMPRINT",FACE,{"disambiguationData":[TD([[makeQuery(id+"F0.imprint","IMPRINT",EDGE,{"derivedFrom":sQuery(id+"F0.wireOp",EDGE,"E1.bottom")}),1.0]])]});
            var Q1;
            Q1=makeQuery(id+"F16.imprint","IMPRINT",FACE,{"disambiguationData":[TD([[makeQuery(id+"F16.imprint","IMPRINT",EDGE,{"derivedFrom":sQuery(id+"F16.wireOp",EDGE,"E79")}),-1.0]])]});
            var Q2;
            {var subQ3=sQuery(id+"F16.wireOp",EDGE,"E89.MirrorCS");Q2=makeQuery(id+"F16.imprint","IMPRINT",FACE,{"disambiguationData":[TD([[makeQuery(id+"F16.imprint","IMPRINT",EDGE,{"derivedFrom":subQ3}),1.0]])]});}
            extrude(context, id + "F17", {"entities" : qUnion([Q0, Q1, Q2]), "depth" : 25 * mm, "offsetDistance" : 25 * mm});
        }
    });
